# Revit family: Crest Boiler FBN2501-6001
name_source: partatom
category: Mechanical Equipment
revit_build: Autodesk Revit 2016 (Build: 20150220_1215(x64)
units: mm (PartAtom-declared; Revit-internal decimal feet)

## family parameters
Always vertical = Yes
Cut with Voids When Loaded = No
OmniClass Number = 23.65.35.11.17
OmniClass Title = Thermodynamic Water Heaters
Part Type = Normal
Room Calculation Point = No
Round Connector Dimension = Use Radius
Shared = No
Work Plane-Based = No

## types (6) — shared parameters
A_HEIGHT = 77 3/4"
Back Clearance = 24"
Description = CREST Condensing Boiler
FUEL TYPE = NATURAL GAS
Front Clearance = 30"
Fuel Type = Natural
Left Clearance = 24"
Manufacturer = Lochinvar
Right Clearance = 24"
SES BIM Studio # = 18 0649 04-1
Top Clearance = 24"
URL = http://www.lochinvar.com
Voltage/Control = 24

## per-type parameters (varying)
- FBN2501: # of Electrical Connections=1; AIR INLET SIZE=8"; Air Inlet Radius=4"; B_WIDTH=35"; Back of Unit to CL of Vent=4 1/4"; Condensate Length from Vent CL=-7 1/2"; Curve Position=7 1/4"; D_Water Outlet Offset=83 3/4"; E_Water Outlet Height=63 3/4"; F_Water Inlet Height=13 1/2"; GALLON CAPACITY=161; GAS CONN SIZE=2"; G_Boiler Drain Height=11 1/4"; Gas Conn Radius=1"; INPUT RATE (BTUH)=2,500,000; K_DEPTH=83 1/4"; L_Depth to Vent=76 1/4"; M_Air Inlet Offset=19 3/4"; N_Air Inlet Offset=9 1/4"; O_Width to Gas=28 3/4"; P_Gas Conn Offset=32"; R_ Vent Offset=7 1/4"; Total Amps=10.2; VENT SIZE=9"; Vent Radius=4 1/2"; Voltage/Heater=120/1PH; WATER CONN SIZE=4"; Water Conn Radius=2"
- FBN3001: # of Electrical Connections=1; AIR INLET SIZE=10"; Air Inlet Radius=5"; B_WIDTH=35"; Back of Unit to CL of Vent=4 3/4"; Condensate Length from Vent CL=-7 1/2"; Curve Position=7 1/4"; D_Water Outlet Offset=83 3/4"; E_Water Outlet Height=63 3/4"; F_Water Inlet Height=13 1/2"; GALLON CAPACITY=181; GAS CONN SIZE=2"; G_Boiler Drain Height=11 1/4"; Gas Conn Radius=1"; INPUT RATE (BTUH)=3,000,000; K_DEPTH=83 1/4"; L_Depth to Vent=76 1/4"; M_Air Inlet Offset=19 3/4"; N_Air Inlet Offset=9 1/4"; O_Width to Gas=28 3/4"; P_Gas Conn Offset=32"; R_ Vent Offset=7 1/4"; Total Amps=13.6; VENT SIZE=10"; Vent Radius=5"; Voltage/Heater=120/1PH; WATER CONN SIZE=4"; Water Conn Radius=2"
- FBN3501: # of Electrical Connections=1; AIR INLET SIZE=10"; Air Inlet Radius=5"; B_WIDTH=42"; Back of Unit to CL of Vent=5"; Condensate Length from Vent CL=-9 1/4"; Curve Position=9"; D_Water Outlet Offset=86 3/4"; E_Water Outlet Height=63 1/2"; F_Water Inlet Height=13 1/4"; GALLON CAPACITY=215; GAS CONN SIZE=2"; G_Boiler Drain Height=11 1/2"; Gas Conn Radius=1"; INPUT RATE (BTUH)=3,500,000; K_DEPTH=91"; L_Depth to Vent=82"; M_Air Inlet Offset=20 1/4"; N_Air Inlet Offset=12 3/4"; O_Width to Gas=35 1/2"; P_Gas Conn Offset=31 3/4"; R_ Vent Offset=8 3/4"; Total Amps=19.7; VENT SIZE=10"; Vent Radius=5"; Voltage/Heater=120/1PH; WATER CONN SIZE=4"; Water Conn Radius=2"
- FBN4001: # of Electrical Connections=3; AIR INLET SIZE=12"; Air Inlet Radius=6"; B_WIDTH=45 1/2"; Back of Unit to CL of Vent=5 1/8"; Condensate Length from Vent CL=-9"; Curve Position=9 7/8"; D_Water Outlet Offset=99"; E_Water Outlet Height=63 1/2"; F_Water Inlet Height=13 3/4"; GALLON CAPACITY=291; GAS CONN SIZE=2 1/2"; G_Boiler Drain Height=11 1/2"; Gas Conn Radius=1 1/4"; INPUT RATE (BTUH)=4,000,000; K_DEPTH=103"; L_Depth to Vent=94"; M_Air Inlet Offset=24 3/4"; N_Air Inlet Offset=13 1/2"; O_Width to Gas=39 1/2"; P_Gas Conn Offset=42 1/4"; R_ Vent Offset=10 1/2"; Total Amps=14; VENT SIZE=12"; Vent Radius=6"; Voltage/Heater=208/3PH; WATER CONN SIZE=4"; Water Conn Radius=2"
- FBN5001: # of Electrical Connections=3; AIR INLET SIZE=12"; Air Inlet Radius=6"; B_WIDTH=46 1/2"; Back of Unit to CL of Vent=6 1/8"; Condensate Length from Vent CL=-9 1/4"; Curve Position=10 1/8"; D_Water Outlet Offset=99 1/2"; E_Water Outlet Height=63 1/2"; F_Water Inlet Height=15"; GALLON CAPACITY=380; GAS CONN SIZE=2 1/2"; G_Boiler Drain Height=11 1/2"; Gas Conn Radius=1 1/4"; INPUT RATE (BTUH)=5,000,000; K_DEPTH=101 3/4"; L_Depth to Vent=92 1/2"; M_Air Inlet Offset=22"; N_Air Inlet Offset=14"; O_Width to Gas=39 3/4"; P_Gas Conn Offset=39 1/2"; R_ Vent Offset=9"; Total Amps=12; VENT SIZE=14"; Vent Radius=7"; Voltage/Heater=208/3PH; WATER CONN SIZE=6"; Water Conn Radius=3"
- FBN6001: # of Electrical Connections=3; AIR INLET SIZE=14"; Air Inlet Radius=7"; B_WIDTH=50"; Back of Unit to CL of Vent=5 1/4"; Condensate Length from Vent CL=-8 7/8"; Curve Position=11"; D_Water Outlet Offset=99 3/4"; E_Water Outlet Height=63 1/4"; F_Water Inlet Height=14 3/4"; GALLON CAPACITY=380; GAS CONN SIZE=2 1/2"; G_Boiler Drain Height=11 1/2"; Gas Conn Radius=1 1/4"; INPUT RATE (BTUH)=6,000,000; K_DEPTH=102 1/2"; L_Depth to Vent=93 1/4"; M_Air Inlet Offset=20"; N_Air Inlet Offset=15 3/4"; O_Width to Gas=43 1/2"; P_Gas Conn Offset=36 1/2"; R_ Vent Offset=9 1/4"; Total Amps=12; VENT SIZE=14"; Vent Radius=7"; Voltage/Heater=208/3PH; WATER CONN SIZE=6"; Water Conn Radius=3"

note: column(s) folded — value = type name in every type: MODEL NO., Model

## geometry (parser evidence)
native form markers: Sweep x2
no freeform markers — native parametric forms only
